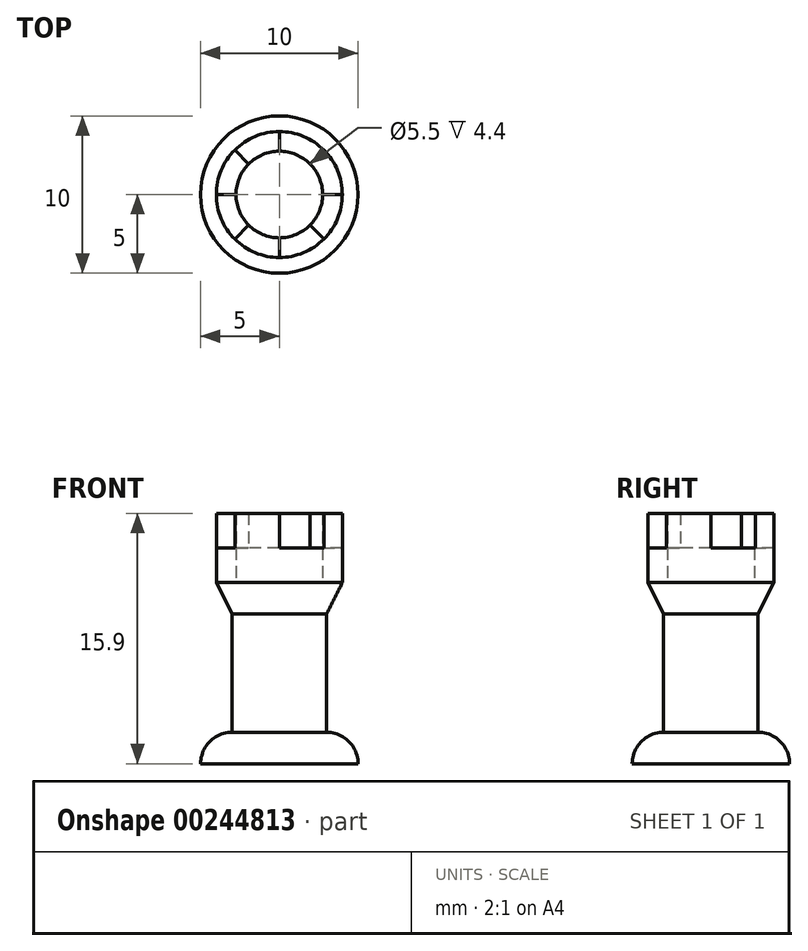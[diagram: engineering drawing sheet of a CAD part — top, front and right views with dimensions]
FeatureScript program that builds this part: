
annotation { "Feature Type Name" : "Feature", "Feature Type Description" : "" }
export const myFeature = defineFeature(function(context is Context, id is Id, definition is map)
    precondition{}
    {
        {
            var Q0;
            Q0=qCreatedBy(makeId("Top.planeOp"),FACE);
            var sketch = newSketch(context, id + "F0", { "sketchPlane" : qUnion([Q0])});
            skCircle(sketch, "E0", {"center": v(0, 0) * mm, "radius": 5 * mm});
            skSolve(sketch);
        }
        {
            var Q0;
            Q0=makeQuery(id+"F0.imprint","IMPRINT",FACE,{"disambiguationData":[TD([[makeQuery(id+"F0.imprint","IMPRINT",EDGE,{"derivedFrom":sQuery(id+"F0.wireOp",EDGE,"E0")}),1.0]])]});
            extrude(context, id + "F1", {"entities" : qUnion([Q0]), "flatOperationType" : FlatOperationType.REMOVE, "offsetDistance" : 25 * mm, "depth" : 2 * mm, "domain" : OperationDomain.MODEL});
        }
        {
            var Q0;
            Q0=makeQuery(id+"F1.opExtrude","CAP_EDGE",EDGE,{"disambiguationData":[OSD([sQuery(id+"F0.wireOp",EDGE,"E0")])],"isStart":false});
            fillet(context, id + "F2", {"entities" : qUnion([Q0]), "radius" : 2 * mm, "tangentPropagation" : true, "defaultsChanged" : false, "vertexSettings" : [], "allowEdgeOverflow" : false});
        }
        {
            var Q0;
            Q0=makeQuery(id+"F1.opExtrude","CAP_FACE",FACE,{"disambiguationData":[OSD([sQuery(id+"F0.wireOp",EDGE,"E0")])],"isStart":false});
            extrude(context, id + "F3", {"entities" : qUnion([Q0]), "operationType" : NewBodyOperationType.ADD, "flatOperationType" : FlatOperationType.REMOVE, "offsetDistance" : 25 * mm, "depth" : 7.5 * mm, "domain" : OperationDomain.MODEL});
        }
        {
            var Q0;
            Q0=makeQuery(id+"F3.opExtrude","CAP_FACE",FACE,{"disambiguationData":[OSD([sQuery(id+"F0.wireOp",EDGE,"E0")])],"isStart":false});
            cPlane(context, id + "F4", {"entities" : qUnion([Q0]), "cplaneType" : CPlaneType.OFFSET, "offset" : 2 * mm, "width" : 150 * mm, "height" : 150 * mm});
        }
        {
            var Q0;
            Q0=qCreatedBy(id+"F4.planeOp",FACE);
            var sketch = newSketch(context, id + "F5", { "sketchPlane" : qUnion([Q0])});
            skCircle(sketch, "E1", {"center": v(0, 0) * mm, "radius": 4 * mm});
            skSolve(sketch);
        }
        {
            var Q0;
            Q0=makeQuery(id+"F5.imprint","IMPRINT",FACE,{"disambiguationData":[TD([[makeQuery(id+"F5.imprint","IMPRINT",EDGE,{"derivedFrom":sQuery(id+"F5.wireOp",EDGE,"E1")}),1.0]])]});
            extrude(context, id + "F6", {"entities" : qUnion([Q0]), "operationType" : NewBodyOperationType.ADD, "oppositeDirection" : true, "depth" : 2 * mm});
        }
        {
            var Q0;
            Q0=makeQuery(id+"F6.opExtrude","CAP_EDGE",EDGE,{"disambiguationData":[OSD([sQuery(id+"F5.wireOp",EDGE,"E1")])],"isStart":false});
            chamfer(context, id + "F7", {"entities" : qUnion([Q0]), "chamferType" : ChamferType.TWO_OFFSETS, "width1" : 2 * mm, "oppositeDirection" : false, "width2" : 1 * mm, "tangentPropagation" : true});
        }
        {
            var Q0;
            Q0=makeQuery(id+"F6.opExtrude","CAP_FACE",FACE,{"disambiguationData":[OSD([sQuery(id+"F5.wireOp",EDGE,"E1")])],"isStart":true});
            var sketch = newSketch(context, id + "F8", { "sketchPlane" : qUnion([Q0])});
            skCircle(sketch, "E2", {"center": v(0, 0) * mm, "radius": 2.75 * mm});
            skCircle(sketch, "E3.cCircle", {"center": v(0, 0) * mm, "radius": 2.75 * mm, "construction": true});
            skLineSegment(sketch, "E3.0", {"start": v(0, 2.75) * mm, "end": v(1.94, 1.94) * mm, "construction": true});
            skLineSegment(sketch, "E3.1", {"start": v(1.94, 1.94) * mm, "end": v(2.75, 0) * mm, "construction": true});
            skLineSegment(sketch, "E3.2", {"start": v(2.75, 0) * mm, "end": v(1.94, -1.94) * mm, "construction": true});
            skLineSegment(sketch, "E3.3", {"start": v(1.94, -1.94) * mm, "end": v(0, -2.75) * mm, "construction": true});
            skLineSegment(sketch, "E3.4", {"start": v(0, -2.75) * mm, "end": v(-1.94, -1.94) * mm, "construction": true});
            skLineSegment(sketch, "E3.5", {"start": v(-1.94, -1.94) * mm, "end": v(-2.75, 0) * mm, "construction": true});
            skLineSegment(sketch, "E3.6", {"start": v(-2.75, 0) * mm, "end": v(-1.94, 1.94) * mm, "construction": true});
            skLineSegment(sketch, "E3.7", {"start": v(-1.94, 1.94) * mm, "end": v(0, 2.75) * mm, "construction": true});
            skCircle(sketch, "E4.cCircle", {"center": v(0, 0) * mm, "radius": 4 * mm, "construction": true});
            skLineSegment(sketch, "E5", {"start": v(0, 2.75) * mm, "end": v(0, 4) * mm});
            skLineSegment(sketch, "E6", {"start": v(-1.94, 1.94) * mm, "end": v(-2.83, 2.83) * mm});
            skLineSegment(sketch, "E7", {"start": v(-2.75, 0) * mm, "end": v(-4, 0) * mm});
            skLineSegment(sketch, "E8", {"start": v(-1.94, -1.94) * mm, "end": v(-2.83, -2.83) * mm});
            skLineSegment(sketch, "E9", {"start": v(0, -2.75) * mm, "end": v(0, -4) * mm});
            skLineSegment(sketch, "E10", {"start": v(1.94, -1.94) * mm, "end": v(2.83, -2.83) * mm});
            skLineSegment(sketch, "E11", {"start": v(2.75, 0) * mm, "end": v(4, 0) * mm});
            skLineSegment(sketch, "E12", {"start": v(1.94, 1.94) * mm, "end": v(2.83, 2.83) * mm});
            skSolve(sketch);
        }
        {
            var Q0;
            {var subQ0=sQuery(id+"F8.wireOp",EDGE,"E10");Q0=makeQuery(id+"F8.imprint","IMPRINT",FACE,{"disambiguationData":[TD([[makeQuery(id+"F8.imprint","IMPRINT",EDGE,{"derivedFrom":subQ0}),1.0]])]});}
            var Q1;
            {var subQ0=sQuery(id+"F8.wireOp",EDGE,"E8");Q1=makeQuery(id+"F8.imprint","IMPRINT",FACE,{"disambiguationData":[TD([[makeQuery(id+"F8.imprint","IMPRINT",EDGE,{"derivedFrom":subQ0}),1.0]])]});}
            var Q2;
            {var subQ0=sQuery(id+"F8.wireOp",EDGE,"E6");Q2=makeQuery(id+"F8.imprint","IMPRINT",FACE,{"disambiguationData":[TD([[makeQuery(id+"F8.imprint","IMPRINT",EDGE,{"derivedFrom":subQ0}),1.0]])]});}
            var Q3;
            {var subQ0=sQuery(id+"F8.wireOp",EDGE,"E5");Q3=makeQuery(id+"F8.imprint","IMPRINT",FACE,{"disambiguationData":[TD([[makeQuery(id+"F8.imprint","IMPRINT",EDGE,{"derivedFrom":subQ0}),-1.0]])]});}
            extrude(context, id + "F9", {"entities" : qUnion([Q0, Q1, Q2, Q3]), "operationType" : NewBodyOperationType.ADD, "flatOperationType" : FlatOperationType.REMOVE, "offsetDistance" : 25 * mm, "depth" : 4.4 * mm, "domain" : OperationDomain.MODEL});
        }
        {
            var Q0;
            {var subQ0=sQuery(id+"F8.wireOp",EDGE,"E5");Q0=makeQuery(id+"F8.imprint","IMPRINT",FACE,{"disambiguationData":[TD([[makeQuery(id+"F8.imprint","IMPRINT",EDGE,{"derivedFrom":subQ0}),1.0]])]});}
            var Q1;
            {var subQ0=sQuery(id+"F8.wireOp",EDGE,"E9");Q1=makeQuery(id+"F8.imprint","IMPRINT",FACE,{"disambiguationData":[TD([[makeQuery(id+"F8.imprint","IMPRINT",EDGE,{"derivedFrom":subQ0}),1.0]])]});}
            var Q2;
            {var subQ0=sQuery(id+"F8.wireOp",EDGE,"E11");Q2=makeQuery(id+"F8.imprint","IMPRINT",FACE,{"disambiguationData":[TD([[makeQuery(id+"F8.imprint","IMPRINT",EDGE,{"derivedFrom":subQ0}),1.0]])]});}
            var Q3;
            {var subQ0=sQuery(id+"F8.wireOp",EDGE,"E7");Q3=makeQuery(id+"F8.imprint","IMPRINT",FACE,{"disambiguationData":[TD([[makeQuery(id+"F8.imprint","IMPRINT",EDGE,{"derivedFrom":subQ0}),1.0]])]});}
            extrude(context, id + "F10", {"entities" : qUnion([Q0, Q1, Q2, Q3]), "operationType" : NewBodyOperationType.ADD, "flatOperationType" : FlatOperationType.REMOVE, "offsetDistance" : 25 * mm, "depth" : 2.2 * mm, "domain" : OperationDomain.MODEL});
        }
    });
